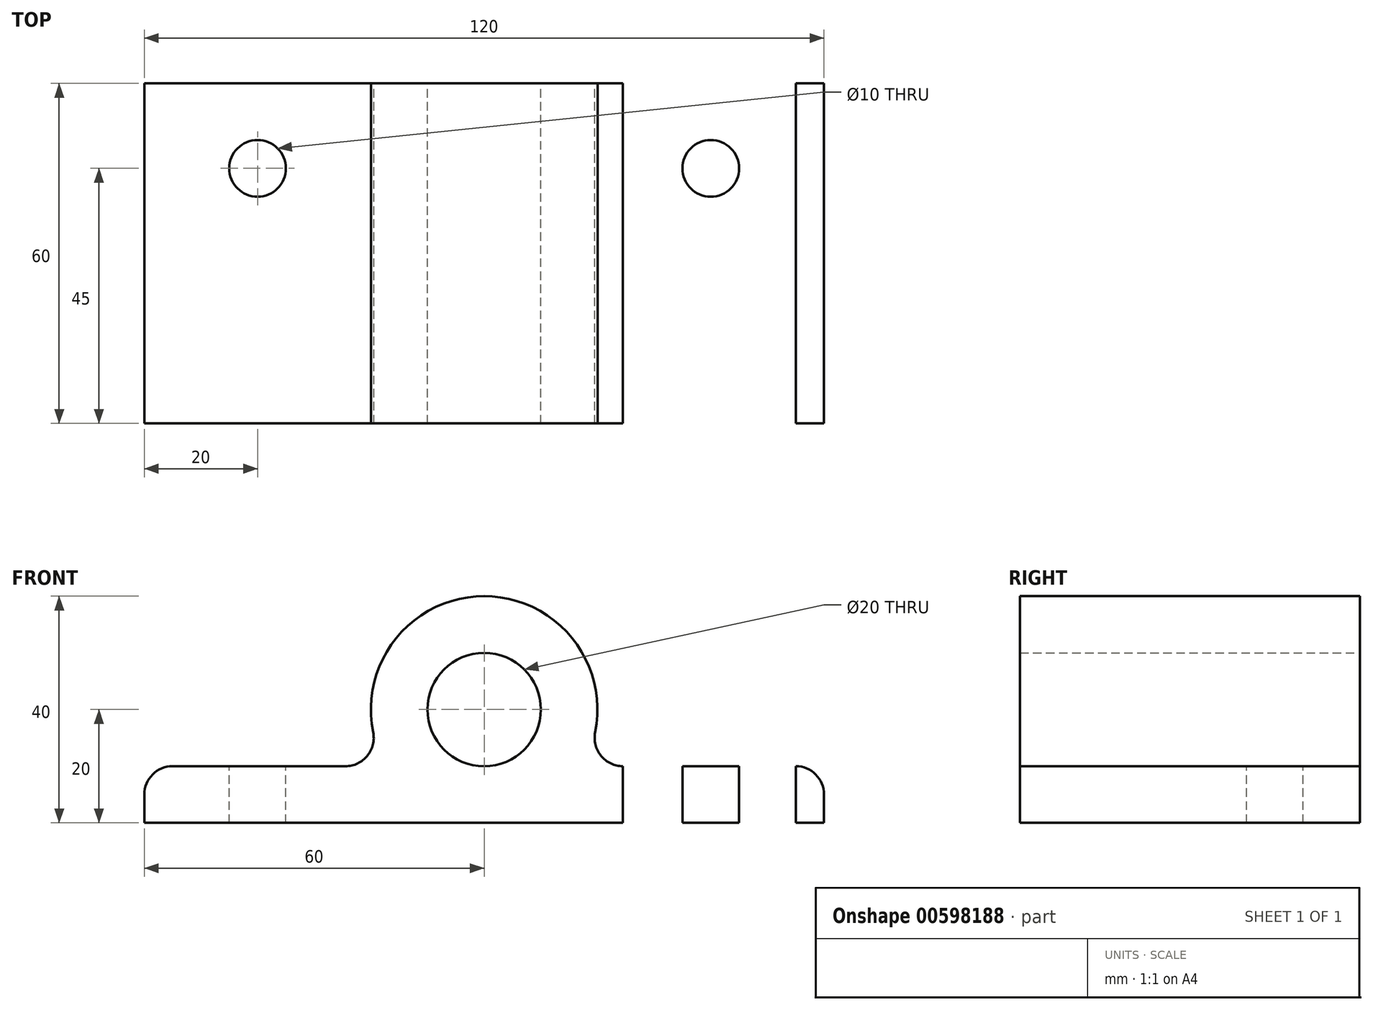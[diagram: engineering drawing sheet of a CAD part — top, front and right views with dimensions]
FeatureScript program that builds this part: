
annotation { "Feature Type Name" : "Feature", "Feature Type Description" : "" }
export const myFeature = defineFeature(function(context is Context, id is Id, definition is map)
    precondition{}
    {
        {
            var Q0;
            Q0=qCreatedBy(makeId("Front.planeOp"),FACE);
            var sketch = newSketch(context, id + "F0", { "sketchPlane" : qUnion([Q0])});
            skCircle(sketch, "E0", {"center": v(0, 0) * mm, "radius": 10 * mm});
            skArc(sketch, "E1", {"start": v(19.6, -4) * mm, "mid": v(0, 20) * mm, "end": v(-19.6, -4) * mm});
            skLineSegment(sketch, "E2", {"start": v(0, 56.44) * mm, "end": v(0, -79.85) * mm, "construction": true});
            skLineSegment(sketch, "E3", {"start": v(-60, -10) * mm, "end": v(-24.5, -10) * mm});
            skLineSegment(sketch, "E4.MirrorCS", {"start": v(60, -10) * mm, "end": v(24.5, -10) * mm});
            skPoint(sketch, "E5.orphan", {"position": v(0, -10) * mm});
            skPoint(sketch, "E6.visualSharp", {"position": v(-17.32, -10) * mm});
            skArc(sketch, "E6.filletArc", {"start": v(-24.5, -10) * mm, "mid": v(-20.62, -8.16) * mm, "end": v(-19.6, -4) * mm});
            skArc(sketch, "E7.MirrorCS", {"start": v(24.5, -10) * mm, "mid": v(20.62, -8.16) * mm, "end": v(19.6, -4) * mm});
            skLineSegment(sketch, "E8", {"start": v(-60, -20) * mm, "end": v(60, -20) * mm});
            skLineSegment(sketch, "E9", {"start": v(-60, -10) * mm, "end": v(-60, -20) * mm});
            skLineSegment(sketch, "E10", {"start": v(60, -10) * mm, "end": v(60, -20) * mm});
            skSolve(sketch);
        }
        {
            var Q0;
            Q0 = qSketchRegion(id + "F0", true);
            extrude(context, id + "F1", {"entities" : qUnion([Q0]), "endBound" : BoundingType.SYMMETRIC, "depth" : 60 * mm, "offsetDistance" : 25 * mm});
        }
        {
            var Q0;
            Q0=makeQuery(id+"F1.opExtrude","SWEPT_EDGE",EDGE,{"disambiguationData":[OSD([sQuery(id+"F0.wireOp",EDGE,"E4.MirrorCS"),sQuery(id+"F0.wireOp",EDGE,"E10")])]});
            var Q1;
            Q1=makeQuery(id+"F1.opExtrude","SWEPT_EDGE",EDGE,{"disambiguationData":[OSD([sQuery(id+"F0.wireOp",EDGE,"E3"),sQuery(id+"F0.wireOp",EDGE,"E9")])]});
            fillet(context, id + "F2", {"entities" : qUnion([Q0, Q1]), "radius" : 5 * mm, "tangentPropagation" : true, "allowEdgeOverflow" : false});
        }
        {
            var Q0;
            Q0=makeQuery(id+"F1.opExtrude","SWEPT_FACE",FACE,{"disambiguationData":[OSD([sQuery(id+"F0.wireOp",EDGE,"E4.MirrorCS")])]});
            var sketch = newSketch(context, id + "F3", { "sketchPlane" : qUnion([Q0])});
            skCircle(sketch, "E11", {"center": v(-40, 15) * mm, "radius": 5 * mm});
            skCircle(sketch, "E12.MirrorC", {"center": v(-40, -15) * mm, "radius": 5 * mm});
            skCircle(sketch, "E13.MirrorC", {"center": v(40, 15) * mm, "radius": 5 * mm});
            skCircle(sketch, "E14.MirrorC", {"center": v(40, -15) * mm, "radius": 5 * mm});
            skSolve(sketch);
        }
        {
            var Q0;
            Q0=makeQuery(id+"F3.imprint","IMPRINT",FACE,{"disambiguationData":[TD([[makeQuery(id+"F3.imprint","IMPRINT",EDGE,{"derivedFrom":sQuery(id+"F3.wireOp",EDGE,"E11")}),1.0]])]});
            var Q1;
            Q1=makeQuery(id+"F3.imprint","IMPRINT",FACE,{"disambiguationData":[TD([[makeQuery(id+"F3.imprint","IMPRINT",EDGE,{"derivedFrom":sQuery(id+"F3.wireOp",EDGE,"E12.MirrorC")}),-1.0]])]});
            var Q2;
            Q2=makeQuery(id+"F3.imprint","IMPRINT",FACE,{"disambiguationData":[TD([[makeQuery(id+"F3.imprint","IMPRINT",EDGE,{"derivedFrom":sQuery(id+"F3.wireOp",EDGE,"E14.MirrorC")}),1.0]])]});
            var Q3;
            Q3=makeQuery(id+"F3.imprint","IMPRINT",FACE,{"disambiguationData":[TD([[makeQuery(id+"F3.imprint","IMPRINT",EDGE,{"derivedFrom":sQuery(id+"F3.wireOp",EDGE,"E13.MirrorC")}),-1.0]])]});
            extrude(context, id + "F4", {"entities" : qUnion([Q0, Q1, Q2, Q3]), "operationType" : NewBodyOperationType.REMOVE, "endBound" : BoundingType.THROUGH_ALL, "oppositeDirection" : true, "depth" : 25 * mm, "offsetDistance" : 25 * mm});
        }
    });
